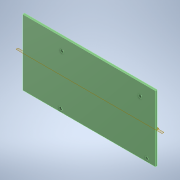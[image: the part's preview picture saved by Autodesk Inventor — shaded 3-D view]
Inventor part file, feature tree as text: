
AUTODESK INVENTOR PART (.ipt)
format: ipt  version: 2021 (Build 250183000, 183)  size: 123,904 bytes
history: native  units: mm
features: sketch x2, extrude x1, hole x1, plane x1, other x1
ambient origin geometry x8: Origin, YZ Plane, XZ Plane, XY Plane, X Axis, Y Axis, Z Axis, Center Point
bodies: Solid1 (feature_tree)
feature tree (6):
  sketch  "Sketch1"  dims[d0=127.0mm d1=63.0mm]
  extrude  "Extrusion1"  Depth=63.0mm
  hole  "Hole1"  [1 undecoded]
  sketch  "Sketch2"  dims[d8=1.8mm d9=0.0mm d10=3.1mm d11=6.0mm d12=4.0mm d13=2.0mm d14=90.0deg d15=8.0mm d16=180.0deg d17=5.08mm d18=30.48mm d19=3.12mm d20=11.47mm d21=37.53mm d22=36.26mm d23=118.81mm d24=112.46mm d25=30.85mm d26=28.0mm d27=20.27mm d28=11.88mm d29=2.85mm]
  plane  "Work Plane1"
  other  "Work Point1"
note: 1 required parameter value undecoded (feature->parameter linkage not recoverable at this tier; creation-order binding heuristic only, values carry confidence <= 0.55)
